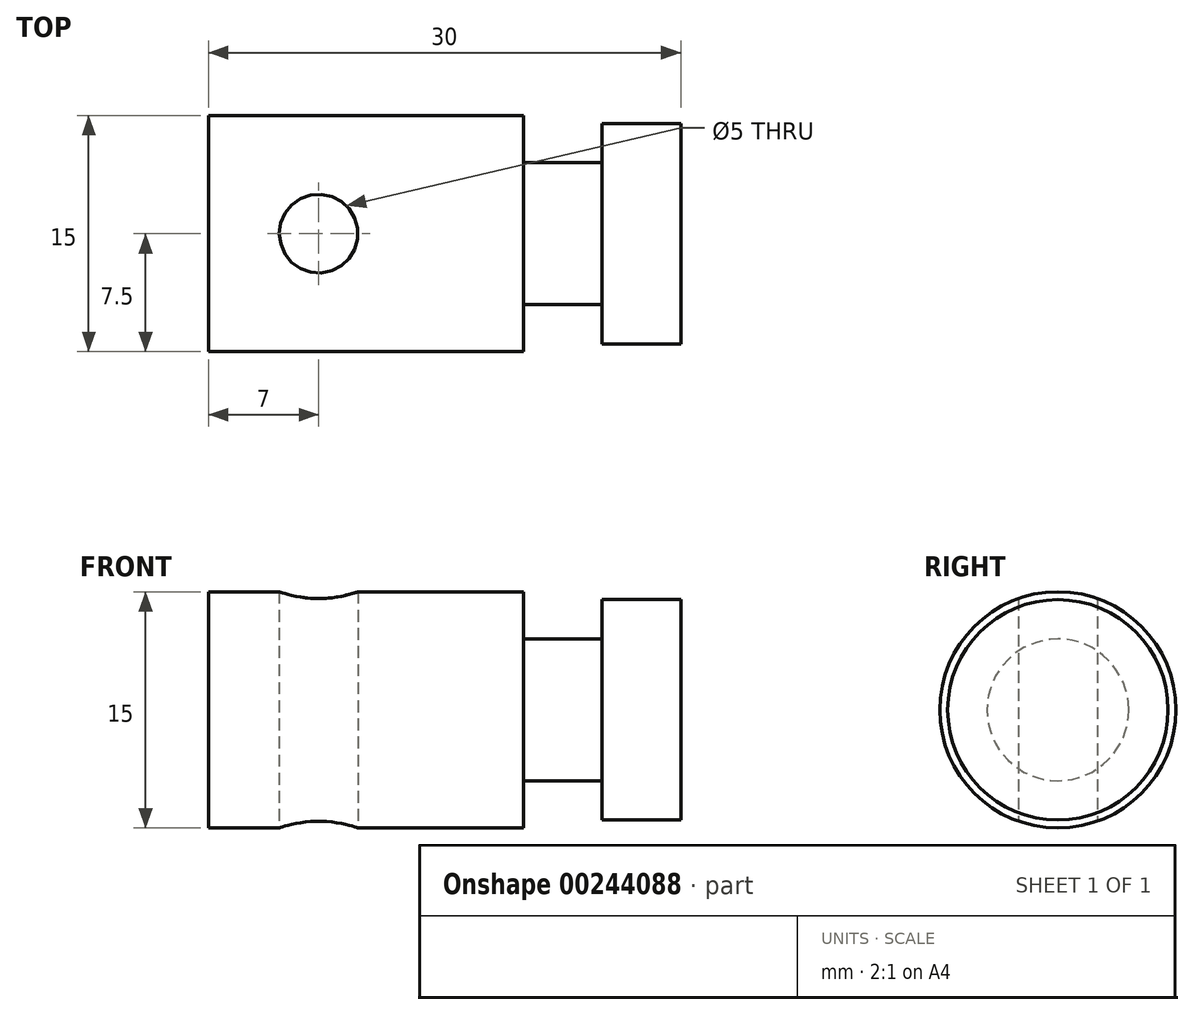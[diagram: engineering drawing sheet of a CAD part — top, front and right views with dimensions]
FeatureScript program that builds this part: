
annotation { "Feature Type Name" : "Feature", "Feature Type Description" : "" }
export const myFeature = defineFeature(function(context is Context, id is Id, definition is map)
    precondition{}
    {
        {
            var Q0;
            Q0=qCreatedBy(makeId("Top.planeOp"),FACE);
            var sketch = newSketch(context, id + "F0", { "sketchPlane" : qUnion([Q0])});
            skLineSegment(sketch, "E0", {"start": v(0, 0) * mm, "end": v(0, 7.5) * mm});
            skLineSegment(sketch, "E1", {"start": v(0, 7.5) * mm, "end": v(20, 7.5) * mm});
            skLineSegment(sketch, "E2", {"start": v(20, 7.5) * mm, "end": v(20, 4.5) * mm});
            skLineSegment(sketch, "E3", {"start": v(20, 4.5) * mm, "end": v(25, 4.5) * mm});
            skLineSegment(sketch, "E4", {"start": v(25, 4.5) * mm, "end": v(25, 7) * mm});
            skLineSegment(sketch, "E5", {"start": v(25, 7) * mm, "end": v(30, 7) * mm});
            skLineSegment(sketch, "E6", {"start": v(30, 7) * mm, "end": v(30, 0) * mm});
            skLineSegment(sketch, "E7", {"start": v(30, 0) * mm, "end": v(0, 0) * mm});
            skSolve(sketch);
        }
        {
            var Q0;
            Q0 = qSketchRegion(id + "F0", true);
            var Q1;
            Q1=sQuery(id+"F0.wireOp",EDGE,"E7");
            revolve(context, id + "F1", {"entities" : qUnion([Q0]), "axis" : qUnion([Q1]), "revolveType" : RevolveType.FULL});
        }
        {
            var Q0;
            Q0=makeQuery(id+"FTopno7x0UGQSbJ_1.splitOp","SPLIT",BODY,{"derivedFrom":makeQuery(id+"F1.opRevolve","SWEPT_BODY",BODY,{"disambiguationData":[OSD([sQuery(id+"F0.wireOp",EDGE,"E0"),sQuery(id+"F0.wireOp",EDGE,"E1"),sQuery(id+"F0.wireOp",EDGE,"E2"),sQuery(id+"F0.wireOp",EDGE,"E3"),sQuery(id+"F0.wireOp",EDGE,"E4"),sQuery(id+"F0.wireOp",EDGE,"E5"),sQuery(id+"F0.wireOp",EDGE,"E6"),sQuery(id+"F0.wireOp",EDGE,"E7")])]})});
            var Q1;
            Q1=makeQuery(id+"FTopno7x0UGQSbJ_1.splitOp","SPLIT",BODY,{"derivedFrom":makeQuery(id+"F1.opRevolve","SWEPT_BODY",BODY,{"disambiguationData":[OSD([sQuery(id+"F0.wireOp",EDGE,"E0"),sQuery(id+"F0.wireOp",EDGE,"E1"),sQuery(id+"F0.wireOp",EDGE,"E2"),sQuery(id+"F0.wireOp",EDGE,"E3"),sQuery(id+"F0.wireOp",EDGE,"E4"),sQuery(id+"F0.wireOp",EDGE,"E5"),sQuery(id+"F0.wireOp",EDGE,"E6"),sQuery(id+"F0.wireOp",EDGE,"E7")])]}),"isFromBackBody":true});
            var Q2;
            Q2=qCreatedBy(makeId("Top.planeOp"),FACE);
            transform(context, id + "F2", {"entities" : qUnion([Q0, Q1]), "transformType" : TransformType.TRANSLATION_DISTANCE, "transformDirection" : qUnion([Q2]), "distance" : 15 / 2 * mm, "makeCopy" : false});
        }
        {
            var Q0;
            Q0=qCreatedBy(makeId("Top.planeOp"),FACE);
            var sketch = newSketch(context, id + "F3", { "sketchPlane" : qUnion([Q0])});
            skPoint(sketch, "E8", {"position": v(7, 0) * mm});
            skSolve(sketch);
        }
        {
            var Q0;
            Q0=sQuery(id+"F3.wireOp",VERTEX,"E8");
            var Q1;
            Q1=makeQuery(id+"FTopno7x0UGQSbJ_1.splitOp","SPLIT",BODY,{"derivedFrom":makeQuery(id+"F1.opRevolve","SWEPT_BODY",BODY,{"disambiguationData":[OSD([sQuery(id+"F0.wireOp",EDGE,"E0"),sQuery(id+"F0.wireOp",EDGE,"E1"),sQuery(id+"F0.wireOp",EDGE,"E2"),sQuery(id+"F0.wireOp",EDGE,"E3"),sQuery(id+"F0.wireOp",EDGE,"E4"),sQuery(id+"F0.wireOp",EDGE,"E5"),sQuery(id+"F0.wireOp",EDGE,"E6"),sQuery(id+"F0.wireOp",EDGE,"E7")])]})});
            var Q2;
            Q2=makeQuery(id+"FTopno7x0UGQSbJ_1.splitOp","SPLIT",BODY,{"derivedFrom":makeQuery(id+"F1.opRevolve","SWEPT_BODY",BODY,{"disambiguationData":[OSD([sQuery(id+"F0.wireOp",EDGE,"E0"),sQuery(id+"F0.wireOp",EDGE,"E1"),sQuery(id+"F0.wireOp",EDGE,"E2"),sQuery(id+"F0.wireOp",EDGE,"E3"),sQuery(id+"F0.wireOp",EDGE,"E4"),sQuery(id+"F0.wireOp",EDGE,"E5"),sQuery(id+"F0.wireOp",EDGE,"E6"),sQuery(id+"F0.wireOp",EDGE,"E7")])]}),"isFromBackBody":true});
            hole(context, id + "F4", {"style" : HoleStyle.SIMPLE, "endStyle" : HoleEndStyle.THROUGH, "oppositeDirection" : true, "standardTappedOrClearance" : lookupTablePath({ "standard" : "ISO", "engagement" : "75%", "pitch" : "1 mm", "size" : "M6", "type" : "Tapped" }), "standardBlindInLast" : lookupTablePath({ "standard" : "ISO", "engagement" : "75%", "pitch" : "1 mm", "size" : "M6", "type" : "Tapped" }), "holeDiameter" : 5 * mm, "locations" : qUnion([Q0]), "scope" : qUnion([Q1, Q2]), "isTappedThrough" : true, "majorDiameter" : 6 * mm, "showTappedDepth" : true});
        }
    });
